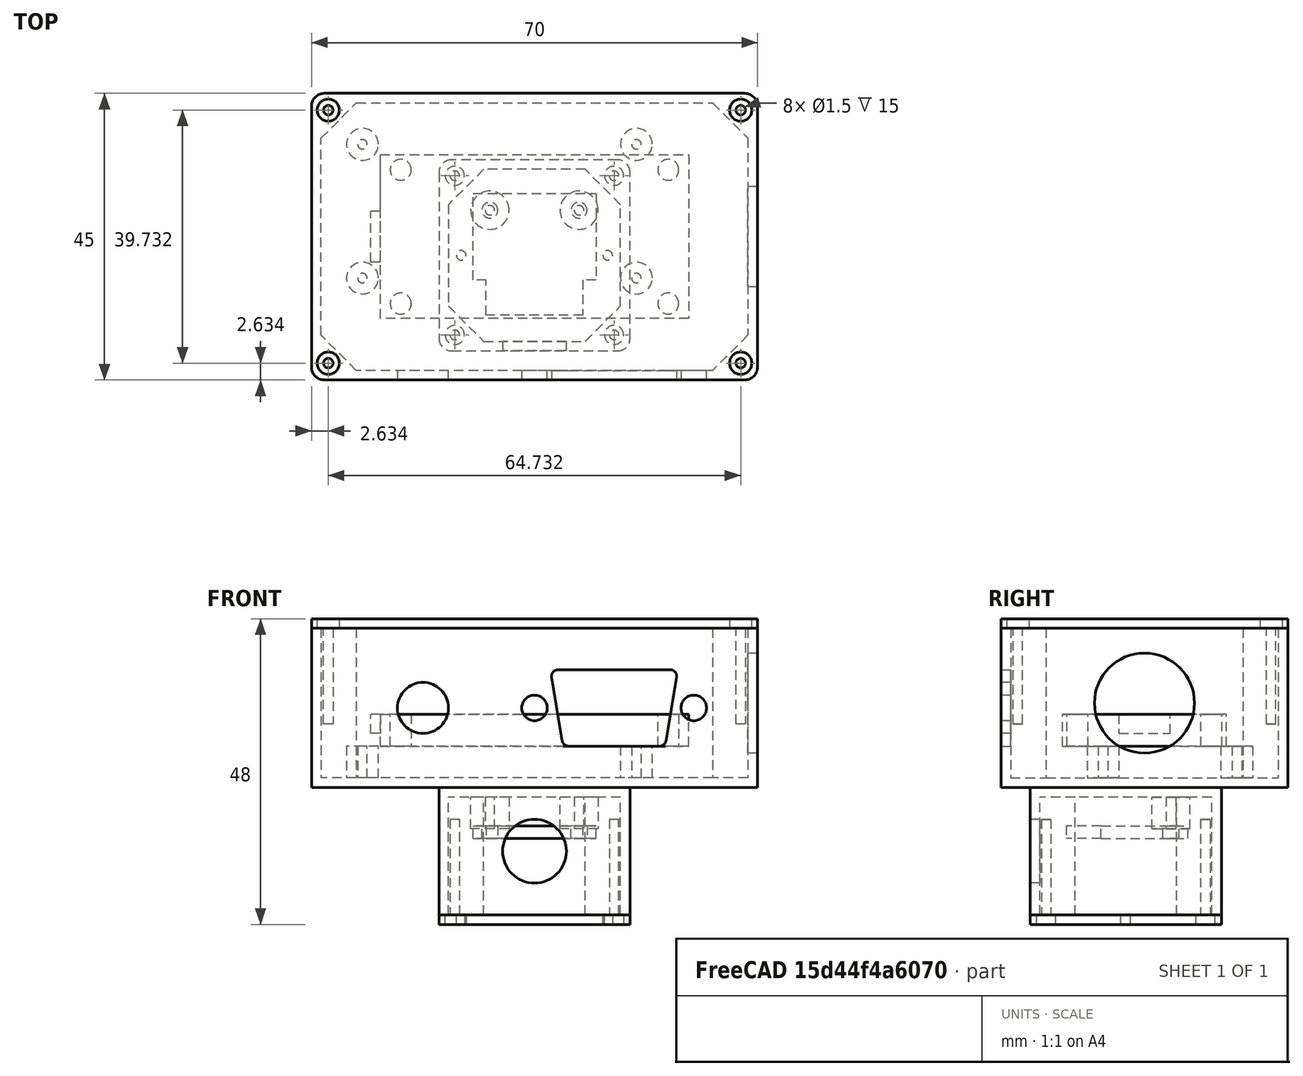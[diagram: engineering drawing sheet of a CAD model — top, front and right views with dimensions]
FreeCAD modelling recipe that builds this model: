
FCSTD DOCUMENT  (FreeCAD 0.18R4 (GitTag))
Label: BaroWifi
License: All rights reserved
LicenseURL: http://en.wikipedia.org/wiki/All_rights_reserved
objects: Sketcher::SketchObject×21, PartDesign::Pad×11, PartDesign::Pocket×10, PartDesign::Body×6, PartDesign::ShapeBinder×4, Mesh::Feature×4, PartDesign::Fillet×2, App::DocumentObjectGroup×2
note: 75 computed .brp shape members not serialized (recipe doc carries the construction recipe); baked Part::Feature solids carry a one-line shape summary decoded from their .brp

FEATURE [Sketcher::SketchObject] Sketch
  MapMode = 5
  Support = -> [XY_Plane]
  sketch-geometry (4):
    g0: LineSegment StartX=-24.2 StartY=12.85 StartZ=0 EndX=24.2 EndY=12.85 EndZ=0
    g1: LineSegment StartX=24.2 StartY=12.85 StartZ=0 EndX=24.2 EndY=-12.85 EndZ=0
    g2: LineSegment StartX=24.2 StartY=-12.85 StartZ=0 EndX=-24.2 EndY=-12.85 EndZ=0
    g3: LineSegment StartX=-24.2 StartY=-12.85 StartZ=0 EndX=-24.2 EndY=12.85 EndZ=0
  constraints (10):
    c: Coincident(g0,g1)
    c: Coincident(g1,g2)
    c: Coincident(g2,g3)
    c: Coincident(g3,g0)
    c: Horizontal(g2)
    c: Vertical(g1)
    c: Symmetric(g2,g0,g-1)
    c: Symmetric(g0,g0,g-2)
    c: DistanceX(g0,g0) = 48.4
    c: DistanceY(g1,g1) = 25.7
FEATURE [PartDesign::Pad] Pad
  Length = 5
  Length2 = 100
  Profile = -> Sketch
  Type = 0
FEATURE [Sketcher::SketchObject] Sketch001
  ExternalGeometry = -> [Pad]
  MapMode = 5
  Placement = pos=(-24.2,0,0) rot=(0.57735,-0.57735,-0.57735;2.0944rad)
  Support = -> [Pad]
  sketch-geometry (4):
    g0: LineSegment StartX=-4 StartY=5 StartZ=0 EndX=4 EndY=5 EndZ=0
    g1: LineSegment StartX=4 StartY=5 StartZ=0 EndX=4 EndY=2 EndZ=0
    g2: LineSegment StartX=4 StartY=2 StartZ=0 EndX=-4 EndY=2 EndZ=0
    g3: LineSegment StartX=-4 StartY=2 StartZ=0 EndX=-4 EndY=5 EndZ=0
  constraints (11):
    c: Coincident(g0,g1)
    c: Coincident(g1,g2)
    c: Coincident(g2,g3)
    c: Coincident(g3,g0)
    c: Horizontal(g2)
    c: Vertical(g1)
    c: Vertical(g3)
    c: Symmetric(g0,g0,g-2)
    c: PointOnObject(g0,g-3)
    c: DistanceY(g1,g1) = 3
    c: DistanceX(g2,g2) = 8
FEATURE [PartDesign::Pad] Pad001
  BaseFeature = -> Pad
  Length = 1.5
  Length2 = 100
  Profile = -> Sketch001
  Type = 0
FEATURE [Sketcher::SketchObject] Sketch002
  MapMode = 5
  Placement = pos=(0,0,5) rot=(0,0,1;0rad)
  Support = -> [Pad001]
  sketch-geometry (4):
    g0: Circle CenterX=-21 CenterY=10.5 CenterZ=0 NormalX=0 NormalY=0 NormalZ=1 AngleXU=0 Radius=1.65
    g1: Circle CenterX=-21 CenterY=-10.5 CenterZ=0 NormalX=0 NormalY=0 NormalZ=1 AngleXU=0 Radius=1.65
    g2: Circle CenterX=21 CenterY=10.5 CenterZ=0 NormalX=0 NormalY=0 NormalZ=1 AngleXU=0 Radius=1.65
    g3: Circle CenterX=21 CenterY=-10.5 CenterZ=0 NormalX=0 NormalY=0 NormalZ=1 AngleXU=0 Radius=1.65
  constraints (9):
    c: Symmetric(g0,g1,g-1)
    c: Symmetric(g2,g3,g-1)
    c: Symmetric(g0,g2,g-2)
    c: DistanceY(g1,g0) = 21
    c: Equal(g0,g2)
    c: Equal(g2,g3)
    c: Equal(g3,g1)
    c: Diameter(g0) = 3.3
    c: DistanceX(g0,g2) = 42
FEATURE [PartDesign::Pocket] Pocket
  BaseFeature = -> Pad001
  Length = 5
  Length2 = 100
  Profile = -> Sketch002
  Type = 1
FEATURE [PartDesign::Body] Body  label="NodeMCU"
  Group = -> [Sketch,Pad,Sketch001,Pad001,Sketch002,Pocket]
  Origin = -> Origin
  Placement = pos=(0,0,6.5) rot=(0,0,1;0rad)
  Tip = -> Pocket
FEATURE [Sketcher::SketchObject] Sketch003
  MapMode = 5
  Support = -> [XY_Plane001]
  sketch-geometry (4):
    g0: LineSegment StartX=-9.65 StartY=6.8 StartZ=0 EndX=9.65 EndY=6.8 EndZ=0
    g1: LineSegment StartX=9.65 StartY=6.8 StartZ=0 EndX=9.65 EndY=-6.8 EndZ=0
    g2: LineSegment StartX=9.65 StartY=-6.8 StartZ=0 EndX=-9.65 EndY=-6.8 EndZ=0
    g3: LineSegment StartX=-9.65 StartY=-6.8 StartZ=0 EndX=-9.65 EndY=6.8 EndZ=0
  constraints (10):
    c: Coincident(g0,g1)
    c: Coincident(g1,g2)
    c: Coincident(g2,g3)
    c: Coincident(g3,g0)
    c: Horizontal(g2)
    c: Vertical(g3)
    c: Symmetric(g0,g1,g-1)
    c: Symmetric(g0,g0,g-2)
    c: DistanceY(g3,g3) = 13.6
    c: DistanceX(g0,g0) = 19.3
FEATURE [PartDesign::Pad] Pad002
  Length = 2
  Length2 = 100
  Profile = -> Sketch003
  Type = 0
FEATURE [Sketcher::SketchObject] Sketch004
  ExternalGeometry = -> [Pad002]
  MapMode = 5
  Placement = pos=(0,0,2) rot=(0,0,1;0rad)
  Support = -> [Pad002]
  sketch-geometry (4):
    g0: LineSegment StartX=-7.6 StartY=-6.8 StartZ=0 EndX=7.6 EndY=-6.8 EndZ=0
    g1: LineSegment StartX=7.6 StartY=-6.8 StartZ=0 EndX=7.6 EndY=-12.3 EndZ=0
    g2: LineSegment StartX=7.6 StartY=-12.3 StartZ=0 EndX=-7.6 EndY=-12.3 EndZ=0
    g3: LineSegment StartX=-7.6 StartY=-12.3 StartZ=0 EndX=-7.6 EndY=-6.8 EndZ=0
  constraints (11):
    c: Coincident(g0,g1)
    c: Coincident(g1,g2)
    c: Coincident(g2,g3)
    c: Coincident(g3,g0)
    c: Horizontal(g2)
    c: Vertical(g1)
    c: Vertical(g3)
    c: PointOnObject(g0,g-3)
    c: Symmetric(g0,g0,g-2)
    c: DistanceY(g3,g3) = 5.5
    c: DistanceX(g2,g2) = 15.2
FEATURE [PartDesign::Pad] Pad003
  BaseFeature = -> Pad002
  Length = 2
  Length2 = 100
  Profile = -> Sketch004
  Reversed = true
  Type = 0
FEATURE [Sketcher::SketchObject] Sketch005
  ExternalGeometry = -> [Pad003]
  MapMode = 5
  Placement = pos=(0,0,2) rot=(0,0,1;0rad)
  Support = -> [Pad003]
  sketch-geometry (2):
    g0: Circle CenterX=-7 CenterY=4.15 CenterZ=0 NormalX=0 NormalY=0 NormalZ=1 AngleXU=0 Radius=1.25
    g1: Circle CenterX=7 CenterY=4.15 CenterZ=0 NormalX=0 NormalY=0 NormalZ=1 AngleXU=0 Radius=1.25
  constraints (5):
    c: Symmetric(g1,g0,g-2)
    c: Diameter(g0) = 2.5
    c: Equal(g0,g1)
    c: DistanceX(g0,g1) = 14
    c: DistanceY(g0,g-3) = 2.65
FEATURE [PartDesign::Pocket] Pocket001
  BaseFeature = -> Pad003
  Length = 5
  Length2 = 100
  Profile = -> Sketch005
  Type = 0
FEATURE [PartDesign::Body] Body001  label="BME680"
  Group = -> [Sketch003,Pad002,Sketch004,Pad003,Sketch005,Pocket001]
  Origin = -> Origin001
  Placement = pos=(0,0,-8) rot=(0,0,1;0rad)
  Tip = -> Pocket001
FEATURE [PartDesign::ShapeBinder] ReferencePocket
  Support = -> [Pocket]
  TraceSupport = false
FEATURE [Sketcher::SketchObject] Sketch006
  ExternalGeometry = -> [ReferencePocket]
  MapMode = 5
  Placement = pos=(0,0,0) rot=(1,0,0;3.14159rad)
  Support = -> [ReferencePocket]
  sketch-geometry (4):
    g0: LineSegment StartX=-35 StartY=22.5 StartZ=0 EndX=35 EndY=22.5 EndZ=0
    g1: LineSegment StartX=35 StartY=22.5 StartZ=0 EndX=35 EndY=-22.5 EndZ=0
    g2: LineSegment StartX=35 StartY=-22.5 StartZ=0 EndX=-35 EndY=-22.5 EndZ=0
    g3: LineSegment StartX=-35 StartY=-22.5 StartZ=0 EndX=-35 EndY=22.5 EndZ=0
  constraints (10):
    c: Coincident(g0,g1)
    c: Coincident(g1,g2)
    c: Coincident(g2,g3)
    c: Coincident(g3,g0)
    c: Horizontal(g2)
    c: Vertical(g3)
    c: Symmetric(g0,g0,g-2)
    c: Symmetric(g0,g1,g-1)
    c: DistanceX(g0,g0) = 70
    c: DistanceY(g1,g1) = 45
FEATURE [PartDesign::Pad] Pad004
  Length = 25
  Length2 = 100
  Profile = -> Sketch006
  Reversed = true
  Type = 0
FEATURE [Sketcher::SketchObject] Sketch007
  ExternalGeometry = -> [Pad004]
  MapMode = 5
  Placement = pos=(0,0,25) rot=(0,0,1;0rad)
  Support = -> [Pad004]
  sketch-geometry (10):
    g0: Circle [constr] CenterX=-32.5 CenterY=20 CenterZ=0 NormalX=0 NormalY=0 NormalZ=1 AngleXU=0 Radius=2.5
    g1: LineSegment StartX=-33.5 StartY=-15.4645 StartZ=0 EndX=-33.5 EndY=15.4645 EndZ=0
    g2: LineSegment StartX=-33.5 StartY=15.4645 StartZ=0 EndX=-27.9645 EndY=21 EndZ=0
    g3: LineSegment StartX=-27.9645 StartY=21 StartZ=0 EndX=27.9645 EndY=21 EndZ=0
    g4: LineSegment StartX=27.9645 StartY=21 StartZ=0 EndX=33.5 EndY=15.4645 EndZ=0
    g5: LineSegment StartX=33.5 StartY=15.4645 StartZ=0 EndX=33.5 EndY=-15.4645 EndZ=0
    g6: LineSegment StartX=33.5 StartY=-15.4645 StartZ=0 EndX=27.9645 EndY=-21 EndZ=0
    g7: LineSegment StartX=27.9645 StartY=-21 StartZ=0 EndX=-27.9645 EndY=-21 EndZ=0
    g8: LineSegment StartX=-27.9645 StartY=-21 StartZ=0 EndX=-33.5 EndY=-15.4645 EndZ=0
    g9: LineSegment [constr] StartX=-30.7322 StartY=18.2322 StartZ=0 EndX=-35 EndY=22.5 EndZ=0
  constraints (24):
    c: Diameter(g0) = 5
    c: Tangent(g0,g-3)
    c: Tangent(g0,g-4)
    c: Coincident(g1,g2)
    c: Coincident(g2,g3)
    c: Coincident(g3,g4)
    c: Coincident(g4,g5)
    c: Coincident(g5,g6)
    c: Coincident(g6,g7)
    c: Coincident(g7,g8)
    c: Coincident(g8,g1)
    c: Symmetric(g1,g1,g-1)
    c: Symmetric(g2,g7,g-1)
    c: Symmetric(g2,g3,g-2)
    c: Symmetric(g1,g4,g-2)
    c: Symmetric(g1,g5,g-2)
    c: Symmetric(g7,g6,g-2)
    c: Tangent(g2,g0)
    c: DistanceY(g2,g-4) = 1.5
    c: DistanceX(g-4,g1) = 1.5
    c: Coincident(g9,g-4)
    c: PointOnObject(g0,g9)
    c: PointOnObject(g9,g2)
    c: Perpendicular(g2,g9)
FEATURE [PartDesign::Pocket] Pocket002
  BaseFeature = -> Pad004
  Length = 23.5
  Length2 = 100
  Profile = -> Sketch007
  Type = 0
FEATURE [PartDesign::ShapeBinder] ReferencePocket001
  Support = -> [Pocket001]
  TraceSupport = false
FEATURE [Sketcher::SketchObject] Sketch014
  ExternalGeometry = -> [ReferencePocket001]
  MapMode = 5
  Placement = pos=(0,0,0) rot=(1,0,0;3.14159rad)
  Support = -> [ReferencePocket001]
  sketch-geometry (4):
    g0: LineSegment StartX=-15 StartY=17.9356 StartZ=0 EndX=15 EndY=17.9356 EndZ=0
    g1: LineSegment StartX=15 StartY=17.9356 StartZ=0 EndX=15 EndY=-12.0644 EndZ=0
    g2: LineSegment StartX=15 StartY=-12.0644 StartZ=0 EndX=-15 EndY=-12.0644 EndZ=0
    g3: LineSegment StartX=-15 StartY=-12.0644 StartZ=0 EndX=-15 EndY=17.9356 EndZ=0
  constraints (9):
    c: Coincident(g0,g1)
    c: Coincident(g1,g2)
    c: Coincident(g2,g3)
    c: Coincident(g3,g0)
    c: Vertical(g1)
    c: Symmetric(g1,g2,g-2)
    c: Symmetric(g0,g0,g-2)
    c: DistanceX(g0,g0) = 30
    c: DistanceY(g2,g0) = 30
FEATURE [PartDesign::Pad] Pad008
  Length = 20
  Length2 = 100
  Profile = -> Sketch014
  Type = 0
FEATURE [Sketcher::SketchObject] Sketch015
  ExternalGeometry = -> [Pad008]
  MapMode = 5
  Placement = pos=(0,0,-20) rot=(1,0,0;3.14159rad)
  Support = -> [Pad008]
  sketch-geometry (18):
    g0: LineSegment StartX=-13.5 StartY=-5.02884 StartZ=0 EndX=-13.5 EndY=10.9001 EndZ=0
    g1: LineSegment StartX=-13.5 StartY=10.9001 StartZ=0 EndX=-7.96447 EndY=16.4356 EndZ=0
    g2: LineSegment StartX=-7.96447 StartY=16.4356 StartZ=0 EndX=7.96447 EndY=16.4356 EndZ=0
    g3: LineSegment StartX=13.5 StartY=-5.02884 StartZ=0 EndX=7.96447 EndY=-10.5644 EndZ=0
    g4: LineSegment StartX=7.96447 StartY=-10.5644 StartZ=0 EndX=-7.96447 EndY=-10.5644 EndZ=0
    g5: LineSegment StartX=-7.96447 StartY=-10.5644 StartZ=0 EndX=-13.5 EndY=-5.02884 EndZ=0
    g6: LineSegment StartX=7.96447 StartY=16.4356 StartZ=0 EndX=13.5 EndY=10.9001 EndZ=0
    g7: LineSegment StartX=13.5 StartY=10.9001 StartZ=0 EndX=13.5 EndY=-5.02884 EndZ=0
    g8: LineSegment [constr] StartX=-15 StartY=2.93562 StartZ=0 EndX=15 EndY=2.93562 EndZ=0
    g9: LineSegment [constr] StartX=-15 StartY=2.93562 StartZ=0 EndX=-15 EndY=-12.0644 EndZ=0
    g10: LineSegment [constr] StartX=-15 StartY=17.9356 StartZ=0 EndX=-10.7322 EndY=13.6679 EndZ=0
    g11: LineSegment [constr] StartX=-13.5 StartY=10.9001 StartZ=0 EndX=-10.7322 EndY=13.6679 EndZ=0
    g12: LineSegment [constr] StartX=-10.7322 StartY=13.6679 StartZ=0 EndX=-7.96447 EndY=16.4356 EndZ=0
    g13: LineSegment [constr] StartX=-15 StartY=17.9356 StartZ=0 EndX=-6.46447 EndY=17.9356 EndZ=0
    g14: LineSegment [constr] StartX=-15 StartY=17.9356 StartZ=0 EndX=-15 EndY=9.40009 EndZ=0
    g15: LineSegment [constr] StartX=-15 StartY=9.40009 StartZ=0 EndX=-6.46447 EndY=17.9356 EndZ=0
    g16: LineSegment [constr] StartX=-15 StartY=17.9356 StartZ=0 EndX=-15 EndY=2.93562 EndZ=0
    g17: Circle [constr] CenterX=-12.5 CenterY=15.4356 CenterZ=0 NormalX=0 NormalY=0 NormalZ=1 AngleXU=0 Radius=2.5
  constraints (45):
    c: Coincident(g0,g1)
    c: Coincident(g1,g2)
    c: Coincident(g3,g4)
    c: Coincident(g4,g5)
    c: Coincident(g0,g5)
    c: Coincident(g6,g7)
    c: Coincident(g7,g3)
    c: Coincident(g6,g2)
    c: Perpendicular(g2,g7)
    c: Symmetric(g1,g2,g-2)
    c: Symmetric(g0,g6,g-2)
    c: PointOnObject(g9,g-5)
    c: Vertical(g9)
    c: PointOnObject(g8,g-6)
    c: PointOnObject(g8,g-4)
    c: Symmetric(g0,g0,g8)
    c: Symmetric(g1,g4,g8)
    c: Symmetric(g0,g3,g-2)
    c: Symmetric(g4,g3,g-2)
    c: DistanceY(g1,g10) = 1.5
    c: DistanceX(g10,g0) = 1.5
    c: PointOnObject(g10,g1)
    c: Perpendicular(g1,g10)
    c: Coincident(g11,g12)
    c: Equal(g12,g11)
    c: Coincident(g12,g1)
    c: Coincident(g11,g0)
    c: Coincident(g10,g11)
    c: Coincident(g15,g13)
    c: Coincident(g13,g14)
    c: Coincident(g14,g15)
    c: PointOnObject(g13,g-3)
    c: Equal(g14,g13)
    c: PointOnObject(g1,g15)
    c: Coincident(g10,g-6)
    c: Coincident(g10,g13)
    c: PointOnObject(g14,g-6)
    c: Coincident(g9,g8)
    c: Coincident(g16,g10)
    c: Coincident(g16,g8)
    c: Equal(g16,g9)
    c: Tangent(g13,g17)
    c: Tangent(g17,g14)
    c: Tangent(g1,g17)
    c: Diameter(g17) = 5
FEATURE [PartDesign::Pocket] Pocket006
  BaseFeature = -> Pad008
  Length = 18.5
  Length2 = 100
  Profile = -> Sketch015
  Type = 0
FEATURE [Sketcher::SketchObject] Sketch016
  ExternalGeometry = -> [ReferencePocket001]
  MapMode = 5
  Placement = pos=(0,0,0) rot=(1,0,0;3.14159rad)
  Support = -> [ReferencePocket001]
  sketch-geometry (2):
    g0: Circle CenterX=-7 CenterY=-4.15 CenterZ=0 NormalX=0 NormalY=0 NormalZ=1 AngleXU=0 Radius=3
    g1: Circle CenterX=7 CenterY=-4.15 CenterZ=0 NormalX=0 NormalY=0 NormalZ=1 AngleXU=0 Radius=3
  constraints (4):
    c: Coincident(g0,g-3)
    c: Coincident(g1,g-4)
    c: Equal(g0,g1)
    c: Diameter(g0) = 6
FEATURE [PartDesign::Pad] Pad009
  BaseFeature = -> Pocket006
  Length = 6.5
  Length2 = 100
  Profile = -> Sketch016
  Type = 0
FEATURE [Sketcher::SketchObject] Sketch017
  ExternalGeometry = -> [Pad009]
  MapMode = 5
  Placement = pos=(0,0,-6.5) rot=(1,0,0;3.14159rad)
  Support = -> [Pad009]
  sketch-geometry (2):
    g0: Circle CenterX=-7 CenterY=-4.15 CenterZ=0 NormalX=0 NormalY=0 NormalZ=1 AngleXU=0 Radius=0.75
    g1: Circle CenterX=7 CenterY=-4.15 CenterZ=0 NormalX=0 NormalY=0 NormalZ=1 AngleXU=0 Radius=0.75
  constraints (4):
    c: Coincident(g0,g-4)
    c: Coincident(g1,g-3)
    c: Equal(g1,g0)
    c: Diameter(g0) = 1.5
FEATURE [PartDesign::Pocket] Pocket007
  BaseFeature = -> Pad009
  Length = 5
  Length2 = 100
  Profile = -> Sketch017
  Type = 0
FEATURE [Sketcher::SketchObject] Sketch018
  ExternalGeometry = -> [Pocket007]
  MapMode = 5
  Placement = pos=(0,0,-20) rot=(1,0,0;3.14159rad)
  Support = -> [Pocket007]
  sketch-geometry (8):
    g0: Circle [constr] CenterX=-12.5 CenterY=15.4356 CenterZ=0 NormalX=0 NormalY=0 NormalZ=1 AngleXU=0 Radius=2.5
    g1: Circle CenterX=-12.5 CenterY=15.4356 CenterZ=0 NormalX=0 NormalY=0 NormalZ=1 AngleXU=0 Radius=0.75
    g2: Circle [constr] CenterX=12.5 CenterY=15.4356 CenterZ=0 NormalX=0 NormalY=0 NormalZ=1 AngleXU=0 Radius=2.5
    g3: Circle [constr] CenterX=12.5 CenterY=-9.56438 CenterZ=0 NormalX=0 NormalY=0 NormalZ=1 AngleXU=0 Radius=2.5
    g4: Circle [constr] CenterX=-12.5 CenterY=-9.56438 CenterZ=0 NormalX=0 NormalY=0 NormalZ=1 AngleXU=0 Radius=2.5
    g5: Circle CenterX=12.5 CenterY=15.4356 CenterZ=0 NormalX=0 NormalY=0 NormalZ=1 AngleXU=0 Radius=0.75
    g6: Circle CenterX=12.5 CenterY=-9.56438 CenterZ=0 NormalX=0 NormalY=0 NormalZ=1 AngleXU=0 Radius=0.75
    g7: Circle CenterX=-12.5 CenterY=-9.56438 CenterZ=0 NormalX=0 NormalY=0 NormalZ=1 AngleXU=0 Radius=0.75
  constraints (20):
    c: Tangent(g0,g-3)
    c: Tangent(g0,g-5)
    c: Tangent(g0,g-4)
    c: Coincident(g1,g0)
    c: Tangent(g4,g-8)
    c: Tangent(g4,g-7)
    c: Tangent(g4,g-5)
    c: Tangent(g3,g-9)
    c: Tangent(g3,g-7)
    c: Tangent(g3,g-6)
    c: Tangent(g2,g-10)
    c: Tangent(g2,g-3)
    c: Tangent(g2,g-6)
    c: Coincident(g7,g4)
    c: Coincident(g5,g2)
    c: Coincident(g6,g3)
    c: Equal(g6,g5)
    c: Equal(g5,g1)
    c: Equal(g1,g7)
    c: Diameter(g1) = 1.5
FEATURE [PartDesign::Pocket] Pocket008
  BaseFeature = -> Pocket007
  Length = 15
  Length2 = 100
  Profile = -> Sketch018
  Type = 0
FEATURE [PartDesign::ShapeBinder] ReferenceFillet001
  TraceSupport = false
FEATURE [Sketcher::SketchObject] Sketch020
  ExternalGeometry = -> [ReferenceFillet001]
  MapMode = 5
  Placement = pos=(0,0,-20) rot=(1,0,0;3.14159rad)
  Support = -> [ReferenceFillet001]
  sketch-geometry (17):
    g0: LineSegment StartX=-13 StartY=17.9356 StartZ=0 EndX=13 EndY=17.9356 EndZ=0
    g1: LineSegment StartX=15 StartY=15.9356 StartZ=0 EndX=15 EndY=-10.0644 EndZ=0
    g2: LineSegment StartX=13 StartY=-12.0644 StartZ=0 EndX=-13 EndY=-12.0644 EndZ=0
    g3: LineSegment StartX=-15 StartY=-10.0644 StartZ=0 EndX=-15 EndY=15.9356 EndZ=0
    g4: ArcOfCircle CenterX=-13 CenterY=15.9356 CenterZ=0 NormalX=0 NormalY=0 NormalZ=1 AngleXU=0 Radius=2 StartAngle=1.5708 EndAngle=3.14159
    g5: ArcOfCircle CenterX=13 CenterY=15.9356 CenterZ=0 NormalX=0 NormalY=0 NormalZ=1 AngleXU=0 Radius=2 StartAngle=0 EndAngle=1.5708
    g6: ArcOfCircle CenterX=13 CenterY=-10.0644 CenterZ=0 NormalX=0 NormalY=0 NormalZ=1 AngleXU=0 Radius=2 StartAngle=4.71239 EndAngle=6.28319
    g7: ArcOfCircle CenterX=-13 CenterY=-10.0644 CenterZ=0 NormalX=0 NormalY=0 NormalZ=1 AngleXU=0 Radius=2 StartAngle=3.14159 EndAngle=4.71239
    g8: Circle CenterX=-12.5 CenterY=15.4356 CenterZ=0 NormalX=0 NormalY=0 NormalZ=1 AngleXU=0 Radius=1.5
    g9: Circle CenterX=12.5 CenterY=15.4356 CenterZ=0 NormalX=0 NormalY=0 NormalZ=1 AngleXU=0 Radius=1.5
    g10: Circle CenterX=12.5 CenterY=-9.56438 CenterZ=0 NormalX=0 NormalY=0 NormalZ=1 AngleXU=0 Radius=1.5
    g11: Circle CenterX=-12.5 CenterY=-9.56438 CenterZ=0 NormalX=0 NormalY=0 NormalZ=1 AngleXU=0 Radius=1.5
    g12: Circle CenterX=-11.5 CenterY=2.93562 CenterZ=0 NormalX=0 NormalY=0 NormalZ=1 AngleXU=0 Radius=0.75
    g13: Circle CenterX=11.5 CenterY=2.93562 CenterZ=0 NormalX=0 NormalY=0 NormalZ=1 AngleXU=0 Radius=0.75
    g14: LineSegment [constr] StartX=-13 StartY=17.9356 StartZ=0 EndX=-13 EndY=2.93562 EndZ=0
    g15: LineSegment [constr] StartX=-13 StartY=2.93562 StartZ=0 EndX=-13 EndY=-12.0644 EndZ=0
    g16: LineSegment [constr] StartX=-13 StartY=2.93562 StartZ=0 EndX=15 EndY=2.93562 EndZ=0
  constraints (41):
    c: Coincident(g7,g3)
    c: Coincident(g3,g4)
    c: Coincident(g4,g0)
    c: Coincident(g0,g5)
    c: Coincident(g5,g1)
    c: Coincident(g1,g6)
    c: Coincident(g6,g2)
    c: Coincident(g2,g7)
    c: Coincident(g7,g-12)
    c: Coincident(g4,g-4)
    c: Coincident(g5,g-9)
    c: Coincident(g6,g-10)
    c: Coincident(g0,g-4)
    c: Coincident(g1,g-9)
    c: Coincident(g1,g-10)
    c: Coincident(g2,g-12)
    c: PointOnObject(g3,g-7)
    c: PointOnObject(g0,g-3)
    c: PointOnObject(g2,g-11)
    c: PointOnObject(g3,g-7)
    c: Coincident(g8,g-6)
    c: Coincident(g9,g-16)
    c: Coincident(g10,g-15)
    c: Coincident(g11,g-13)
    c: Equal(g11,g8)
    c: Equal(g8,g9)
    c: Equal(g9,g10)
    c: Diameter(g8) = 3
    c: Equal(g12,g13)
    c: Diameter(g12) = 1.5
    c: Symmetric(g12,g13,g-2)
    c: Coincident(g14,g15)
    c: Equal(g14,g15)
    c: Parallel(g14,g15)
    c: Coincident(g14,g0)
    c: Coincident(g15,g2)
    c: Coincident(g16,g14)
    c: PointOnObject(g16,g1)
    c: Perpendicular(g14,g16)
    c: PointOnObject(g13,g16)
    c: DistanceX(g12,g13) = 23
FEATURE [PartDesign::Pad] Pad010
  Length = 1.5
  Length2 = 100
  Profile = -> Sketch020
  Type = 0
FEATURE [PartDesign::Body] Body005  label="Capot BME"
  Group = -> [ReferenceFillet001,Sketch020,Pad010]
  Origin = -> Origin005
  Tip = -> Pad010
FEATURE [Mesh::Feature] Mesh003  label="Capot BME (Meshed)"
FEATURE [Sketcher::SketchObject] Sketch008
  ExternalGeometry = -> [Pocket002]
  MapMode = 5
  Placement = pos=(0,0,0) rot=(1,0,0;3.14159rad)
  Support = -> [ReferencePocket]
  sketch-geometry (12):
    g0: Circle CenterX=-27 CenterY=6.5 CenterZ=0 NormalX=0 NormalY=0 NormalZ=1 AngleXU=0 Radius=0.75
    g1: Circle CenterX=16 CenterY=6.5 CenterZ=0 NormalX=0 NormalY=0 NormalZ=1 AngleXU=0 Radius=0.75
    g2: Circle CenterX=-27 CenterY=-14.5 CenterZ=0 NormalX=0 NormalY=0 NormalZ=1 AngleXU=0 Radius=0.75
    g3: Circle CenterX=16 CenterY=-14.5 CenterZ=0 NormalX=0 NormalY=0 NormalZ=1 AngleXU=0 Radius=0.75
    g4: LineSegment [constr] StartX=-27 StartY=6.5 StartZ=0 EndX=16 EndY=6.5 EndZ=0
    g5: LineSegment [constr] StartX=16 StartY=6.5 StartZ=0 EndX=16 EndY=-14.5 EndZ=0
    g6: LineSegment [constr] StartX=16 StartY=-14.5 StartZ=0 EndX=-27 EndY=-14.5 EndZ=0
    g7: LineSegment [constr] StartX=-27 StartY=-14.5 StartZ=0 EndX=-27 EndY=6.5 EndZ=0
    g8: Circle CenterX=-27 CenterY=6.5 CenterZ=0 NormalX=0 NormalY=0 NormalZ=1 AngleXU=0 Radius=2.5
    g9: Circle CenterX=16 CenterY=6.5 CenterZ=0 NormalX=0 NormalY=0 NormalZ=1 AngleXU=0 Radius=2.5
    g10: Circle CenterX=16 CenterY=-14.5 CenterZ=0 NormalX=0 NormalY=0 NormalZ=1 AngleXU=0 Radius=2.5
    g11: Circle CenterX=-27 CenterY=-14.5 CenterZ=0 NormalX=0 NormalY=0 NormalZ=1 AngleXU=0 Radius=2.5
  constraints (28):
    c: Equal(g0,g1)
    c: Equal(g1,g2)
    c: Equal(g2,g3)
    c: Coincident(g4,g5)
    c: Coincident(g5,g6)
    c: Coincident(g6,g7)
    c: Coincident(g7,g4)
    c: Horizontal(g4)
    c: Horizontal(g6)
    c: Vertical(g5)
    c: Vertical(g7)
    c: DistanceX(g4,g4) = 43
    c: DistanceY(g7,g7) = 21
    c: Coincident(g4,g0)
    c: Coincident(g1,g4)
    c: Coincident(g3,g5)
    c: Coincident(g2,g6)
    c: Diameter(g0) = 1.5
    c: Equal(g8,g9)
    c: Equal(g9,g10)
    c: Equal(g10,g11)
    c: Diameter(g8) = 5
    c: Coincident(g8,g0)
    c: Coincident(g9,g1)
    c: Coincident(g10,g3)
    c: Coincident(g11,g2)
    c: DistanceX(g-4,g2) = 8
    c: DistanceY(g-4,g2) = 8
FEATURE [PartDesign::Pad] Pad005
  BaseFeature = -> Pocket002
  Length = 6.5
  Length2 = 100
  Profile = -> Sketch008
  Reversed = true
  Type = 0
FEATURE [Sketcher::SketchObject] Sketch009
  ExternalGeometry = -> [Pad005]
  MapMode = 5
  Placement = pos=(33.5,0,0) rot=(0.57735,-0.57735,-0.57735;2.0944rad)
  Support = -> [Pad005]
  sketch-geometry (4):
    g0: Circle CenterX=-5e-16 CenterY=13.25 CenterZ=0 NormalX=0 NormalY=0 NormalZ=1 AngleXU=0 Radius=7.85
    g1: LineSegment [constr] StartX=15.4645 StartY=25 StartZ=0 EndX=-15.4645 EndY=1.5 EndZ=0
    g2: LineSegment [constr] StartX=-15.4645 StartY=25 StartZ=0 EndX=15.4645 EndY=1.5 EndZ=0
    g3: GeomPoint X=-5e-16 Y=13.25 Z=0
  constraints (8):
    c: Coincident(g0,g3)
    c: Diameter(g0) = 15.7
    c: PointOnObject(g0,g2)
    c: PointOnObject(g0,g1)
    c: Coincident(g2,g-5)
    c: Coincident(g1,g-6)
    c: Coincident(g2,g-6)
    c: Coincident(g1,g-5)
FEATURE [PartDesign::Pocket] Pocket003
  BaseFeature = -> Pad005
  Length = 5
  Length2 = 100
  Profile = -> Sketch009
  Type = 0
FEATURE [Sketcher::SketchObject] Sketch010
  ExternalGeometry = -> [Pocket003]
  MapMode = 5
  Placement = pos=(0,-22.5,0) rot=(1,0,0;1.5708rad)
  Support = -> [Pocket003]
  sketch-geometry (16):
    g0: GeomPoint X=0 Y=25 Z=0
    g1: LineSegment [constr] StartX=-35 StartY=25 StartZ=0 EndX=0 EndY=0 EndZ=0
    g2: LineSegment [constr] StartX=0 StartY=25 StartZ=0 EndX=-35 EndY=0 EndZ=0
    g3: GeomPoint X=-17.5 Y=12.5 Z=0
    g4: Circle CenterX=-17.5 CenterY=12.5 CenterZ=0 NormalX=0 NormalY=0 NormalZ=1 AngleXU=0 Radius=4
    g5: LineSegment [constr] StartX=0 StartY=25 StartZ=0 EndX=35 EndY=0 EndZ=0
    g6: LineSegment [constr] StartX=35 StartY=25 StartZ=0 EndX=0 EndY=0 EndZ=0
    g7: LineSegment [constr] StartX=12.5 StartY=25 StartZ=0 EndX=12.5 EndY=0 EndZ=0
    g8: LineSegment StartX=2.5 StartY=18.5 StartZ=0 EndX=22.5 EndY=18.5 EndZ=0
    g9: LineSegment StartX=22.5 StartY=18.5 StartZ=0 EndX=20.5 EndY=6.5 EndZ=0
    g10: LineSegment StartX=20.5 StartY=6.5 StartZ=0 EndX=4.5 EndY=6.5 EndZ=0
    g11: LineSegment StartX=4.5 StartY=6.5 StartZ=0 EndX=2.5 EndY=18.5 EndZ=0
    g12: Circle CenterX=0 CenterY=12.5 CenterZ=0 NormalX=0 NormalY=0 NormalZ=1 AngleXU=0 Radius=2
    g13: Circle CenterX=25 CenterY=12.5 CenterZ=0 NormalX=0 NormalY=0 NormalZ=1 AngleXU=0 Radius=2
    g14: LineSegment [constr] StartX=2.5 StartY=6.5 StartZ=0 EndX=22.5 EndY=6.5 EndZ=0
    g15: LineSegment [constr] StartX=0 StartY=12.5 StartZ=0 EndX=25 EndY=12.5 EndZ=0
  constraints (37):
    c: PointOnObject(g0,g-2)
    c: PointOnObject(g0,g-3)
    c: Coincident(g1,g-4)
    c: Coincident(g0,g2)
    c: Coincident(g1,g-1)
    c: Coincident(g2,g-4)
    c: PointOnObject(g3,g2)
    c: PointOnObject(g3,g1)
    c: Coincident(g4,g3)
    c: Diameter(g4) = 8
    c: Coincident(g5,g0)
    c: Coincident(g6,g-3)
    c: Coincident(g5,g-5)
    c: Coincident(g6,g-1)
    c: PointOnObject(g7,g-3)
    c: PointOnObject(g7,g-1)
    c: Coincident(g8,g9)
    c: Coincident(g9,g10)
    c: Coincident(g10,g11)
    c: Coincident(g11,g8)
    c: Symmetric(g8,g8,g7)
    c: Symmetric(g10,g9,g7)
    c: Symmetric(g12,g13,g7)
    c: Equal(g12,g13)
    c: Diameter(g12) = 4
    c: DistanceX(g12,g13) = 25
    c: DistanceX(g8,g8) = 20
    c: DistanceX(g10,g9) = 16
    c: DistanceY(g9,g8) = 12
    c: PointOnObject(g10,g14)
    c: PointOnObject(g12,g-2)
    c: Parallel(g8,g-3)
    c: Coincident(g15,g13)
    c: Coincident(g15,g12)
    c: Symmetric(g8,g14,g15)
    c: Symmetric(g8,g14,g15)
    c: PointOnObject(g3,g15)
FEATURE [PartDesign::Pocket] Pocket004
  BaseFeature = -> Pocket003
  Length = 5
  Length2 = 100
  Profile = -> Sketch010
  Type = 0
FEATURE [Sketcher::SketchObject] Sketch011
  ExternalGeometry = -> [Pocket004]
  MapMode = 5
  Placement = pos=(0,-22.5,0) rot=(1,0,0;1.5708rad)
  Support = -> [Pocket004]
  sketch-geometry (12):
    g0: ArcOfCircle CenterX=21.3195 CenterY=17.5 CenterZ=0 NormalX=0 NormalY=0 NormalZ=1 AngleXU=0 Radius=1 StartAngle=6.11804 EndAngle=7.85398
    g1: ArcOfCircle CenterX=3.68046 CenterY=17.5 CenterZ=0 NormalX=0 NormalY=0 NormalZ=1 AngleXU=0 Radius=1 StartAngle=1.5708 EndAngle=3.30674
    g2: ArcOfCircle CenterX=5.34713 CenterY=7.5 CenterZ=0 NormalX=0 NormalY=0 NormalZ=1 AngleXU=0 Radius=1 StartAngle=3.30675 EndAngle=4.71238
    g3: ArcOfCircle CenterX=19.6529 CenterY=7.5 CenterZ=0 NormalX=0 NormalY=0 NormalZ=1 AngleXU=0 Radius=1 StartAngle=4.71239 EndAngle=6.11804
    g4: LineSegment StartX=21.3195 StartY=18.5 StartZ=0 EndX=22.5 EndY=18.5 EndZ=0
    g5: LineSegment StartX=22.5 StartY=18.5 StartZ=0 EndX=22.3059 EndY=17.3356 EndZ=0
    g6: LineSegment StartX=20.6393 StartY=7.3356 StartZ=0 EndX=20.5 EndY=6.5 EndZ=0
    g7: LineSegment StartX=20.5 StartY=6.5 StartZ=0 EndX=19.6529 EndY=6.5 EndZ=0
    g8: LineSegment StartX=4.36073 StartY=7.33559 StartZ=0 EndX=4.5 EndY=6.5 EndZ=0
    g9: LineSegment StartX=4.5 StartY=6.5 StartZ=0 EndX=5.34712 EndY=6.5 EndZ=0
    g10: LineSegment StartX=3.68046 StartY=18.5 StartZ=0 EndX=2.5 EndY=18.5 EndZ=0
    g11: LineSegment StartX=2.5 StartY=18.5 StartZ=0 EndX=2.69407 EndY=17.3356 EndZ=0
  constraints (34):
    c: Radius(g0) = 1
    c: Equal(g1,g0)
    c: Equal(g0,g3)
    c: Equal(g3,g2)
    c: PointOnObject(g1,g-3)
    c: PointOnObject(g1,g-4)
    c: PointOnObject(g0,g-3)
    c: PointOnObject(g0,g-6)
    c: PointOnObject(g3,g-6)
    c: PointOnObject(g2,g-5)
    c: PointOnObject(g2,g-4)
    c: Coincident(g5,g-6)
    c: Coincident(g5,g4)
    c: Coincident(g4,g0)
    c: Coincident(g5,g0)
    c: Equal(g5,g4)
    c: Coincident(g7,g3)
    c: Coincident(g7,g6)
    c: Coincident(g7,g-6)
    c: Equal(g6,g7)
    c: Coincident(g9,g2)
    c: Coincident(g9,g8)
    c: Coincident(g9,g-5)
    c: Coincident(g8,g2)
    c: Equal(g8,g9)
    c: Coincident(g11,g-4)
    c: Coincident(g11,g10)
    c: Equal(g10,g11)
    c: Tangent(g10,g1) = -1.5708
    c: Tangent(g11,g1) = -1.5708
    c: Tangent(g0,g-3)
    c: Tangent(g6,g3) = 1.5708
    c: Tangent(g-5,g3)
    c: Tangent(g2,g-4)
FEATURE [PartDesign::Pad] Pad006
  BaseFeature = -> Pocket004
  Length = 1.5
  Length2 = 100
  Profile = -> Sketch011
  Reversed = true
  Type = 0
FEATURE [PartDesign::Fillet] Fillet
  Base = -> Pad006 [Edge4,Edge1,Edge39,Edge20]
  BaseFeature = -> Pad006
  Radius = 2
FEATURE [Sketcher::SketchObject] Sketch012
  ExternalGeometry = -> [Fillet]
  MapMode = 5
  Placement = pos=(0,0,25) rot=(0,0,1;0rad)
  Support = -> [Fillet]
  sketch-geometry (9):
    g0: LineSegment [constr] StartX=-33 StartY=22.5 StartZ=0 EndX=-27.9645 EndY=21 EndZ=0
    g1: LineSegment [constr] StartX=-33 StartY=22.5 StartZ=0 EndX=-35 EndY=20.5 EndZ=0
    g2: LineSegment [constr] StartX=-35 StartY=20.5 StartZ=0 EndX=-33.5 EndY=15.4645 EndZ=0
    g3: LineSegment [constr] StartX=-30.7322 StartY=18.2322 StartZ=0 EndX=-32.3661 EndY=19.8661 EndZ=0
    g4: LineSegment [constr] StartX=-32.3661 StartY=19.8661 StartZ=0 EndX=-34 EndY=21.5 EndZ=0
    g5: Circle CenterX=-32.3661 CenterY=19.8661 CenterZ=0 NormalX=0 NormalY=0 NormalZ=1 AngleXU=0 Radius=0.75
    g6: Circle CenterX=32.3661 CenterY=19.8661 CenterZ=0 NormalX=0 NormalY=0 NormalZ=1 AngleXU=0 Radius=0.75
    g7: Circle CenterX=32.3661 CenterY=-19.8661 CenterZ=0 NormalX=0 NormalY=0 NormalZ=1 AngleXU=0 Radius=0.75
    g8: Circle CenterX=-32.3661 CenterY=-19.8661 CenterZ=0 NormalX=0 NormalY=0 NormalZ=1 AngleXU=0 Radius=0.75
  constraints (21):
    c: Coincident(g1,g0)
    c: Coincident(g0,g-6)
    c: Coincident(g2,g1)
    c: Coincident(g2,g-6)
    c: Coincident(g2,g-4)
    c: Coincident(g0,g-4)
    c: Coincident(g3,g4)
    c: PointOnObject(g4,g1)
    c: Parallel(g4,g3)
    c: PointOnObject(g-6,g4)
    c: PointOnObject(g3,g-4)
    c: Equal(g3,g4)
    c: Perpendicular(g-4,g3)
    c: Equal(g8,g7)
    c: Equal(g7,g6)
    c: Equal(g6,g5)
    c: Diameter(g5) = 1.5
    c: Coincident(g5,g3)
    c: Symmetric(g5,g6,g-2)
    c: Symmetric(g5,g8,g-1)
    c: Symmetric(g8,g7,g-2)
FEATURE [PartDesign::Pocket] Pocket005
  BaseFeature = -> Fillet
  Length = 15
  Length2 = 100
  Profile = -> Sketch012
  Type = 0
FEATURE [PartDesign::Body] Body002  label="CorpsBoiteMCU"
  Group = -> [ReferencePocket,Sketch006,Pad004,Sketch007,Pocket002,Sketch008,Pad005,Sketch009,Pocket003,Sketch010,Pocket004,Sketch011,Pad006,Fillet,Sketch012,Pocket005]
  Origin = -> Origin002
  Tip = -> Pocket005
FEATURE [PartDesign::ShapeBinder] ReferencePocket005
  Support = -> [Pocket005]
  TraceSupport = false
FEATURE [Sketcher::SketchObject] Sketch013
  ExternalGeometry = -> [ReferencePocket005]
  MapMode = 5
  Placement = pos=(0,0,25) rot=(0,0,1;0rad)
  Support = -> [ReferencePocket005]
  sketch-geometry (12):
    g0: LineSegment StartX=-33 StartY=22.5 StartZ=0 EndX=33 EndY=22.5 EndZ=0
    g1: LineSegment StartX=35 StartY=20.5 StartZ=0 EndX=35 EndY=-20.5 EndZ=0
    g2: LineSegment StartX=33 StartY=-22.5 StartZ=0 EndX=-33 EndY=-22.5 EndZ=0
    g3: LineSegment StartX=-35 StartY=-20.5 StartZ=0 EndX=-35 EndY=20.5 EndZ=0
    g4: ArcOfCircle CenterX=-33 CenterY=20.5 CenterZ=0 NormalX=0 NormalY=0 NormalZ=1 AngleXU=0 Radius=2 StartAngle=1.5708 EndAngle=3.14159
    g5: ArcOfCircle CenterX=33 CenterY=20.5 CenterZ=0 NormalX=0 NormalY=0 NormalZ=1 AngleXU=0 Radius=2 StartAngle=6.28318 EndAngle=7.85398
    g6: ArcOfCircle CenterX=33 CenterY=-20.5 CenterZ=0 NormalX=0 NormalY=0 NormalZ=1 AngleXU=0 Radius=2 StartAngle=4.71238 EndAngle=6.28319
    g7: ArcOfCircle CenterX=-33 CenterY=-20.5 CenterZ=0 NormalX=0 NormalY=0 NormalZ=1 AngleXU=0 Radius=2 StartAngle=3.14159 EndAngle=4.71239
    g8: Circle CenterX=-32.3661 CenterY=19.8661 CenterZ=0 NormalX=0 NormalY=0 NormalZ=1 AngleXU=0 Radius=1.75
    g9: Circle CenterX=32.3661 CenterY=19.8661 CenterZ=0 NormalX=0 NormalY=0 NormalZ=1 AngleXU=0 Radius=1.75
    g10: Circle CenterX=-32.3661 CenterY=-19.8661 CenterZ=0 NormalX=0 NormalY=0 NormalZ=1 AngleXU=0 Radius=1.75
    g11: Circle CenterX=32.3661 CenterY=-19.8661 CenterZ=0 NormalX=0 NormalY=0 NormalZ=1 AngleXU=0 Radius=1.75
  constraints (28):
    c: Coincident(g7,g3)
    c: Coincident(g7,g2)
    c: Coincident(g2,g6)
    c: Coincident(g6,g1)
    c: Coincident(g1,g5)
    c: Coincident(g5,g0)
    c: Coincident(g0,g4)
    c: Coincident(g4,g3)
    c: Coincident(g-5,g4)
    c: Coincident(g5,g-9)
    c: Coincident(g6,g-12)
    c: PointOnObject(g0,g-4)
    c: Coincident(g3,g-6)
    c: Coincident(g0,g-9)
    c: PointOnObject(g1,g-10)
    c: Coincident(g1,g-12)
    c: PointOnObject(g2,g-11)
    c: Coincident(g2,g-13)
    c: PointOnObject(g3,g-6)
    c: Coincident(g7,g-13)
    c: Coincident(g8,g-3)
    c: Coincident(g9,g-8)
    c: Coincident(g11,g-16)
    c: Coincident(g10,g-15)
    c: Equal(g10,g11)
    c: Equal(g11,g9)
    c: Equal(g9,g8)
    c: Diameter(g8) = 3.5
FEATURE [PartDesign::Pad] Pad007
  Length = 1.5
  Length2 = 100
  Profile = -> Sketch013
  Type = 0
FEATURE [PartDesign::Body] Body003  label="CapotMCU"
  Group = -> [ReferencePocket005,Sketch013,Pad007]
  Origin = -> Origin003
  Tip = -> Pad007
FEATURE [App::DocumentObjectGroup] Group  label="GoupeNodeMCU"
  Group = -> [Body003,Body002,Body]
FEATURE [Mesh::Feature] Mesh  label="CapotMCU (Meshed)"
FEATURE [Mesh::Feature] Mesh006  label="CorpsBoiteMCU (Meshed)"
FEATURE [Sketcher::SketchObject] Sketch021
  ExternalGeometry = -> [Pocket008]
  MapMode = 5
  Placement = pos=(0,-17.9356,0) rot=(1,0,0;1.5708rad)
  Support = -> [Pocket008]
  sketch-geometry (3):
    g0: LineSegment [constr] StartX=-15 StartY=0 StartZ=0 EndX=15 EndY=-20 EndZ=0
    g1: LineSegment [constr] StartX=15 StartY=0 StartZ=0 EndX=-15 EndY=-20 EndZ=0
    g2: Circle CenterX=-5e-16 CenterY=-10 CenterZ=0 NormalX=0 NormalY=0 NormalZ=1 AngleXU=0 Radius=5
  constraints (7):
    c: Coincident(g0,g-3)
    c: Coincident(g1,g-5)
    c: Coincident(g1,g-4)
    c: Coincident(g0,g-5)
    c: Diameter(g2) = 10
    c: PointOnObject(g2,g1)
    c: PointOnObject(g2,g0)
FEATURE [PartDesign::Pocket] Pocket009
  BaseFeature = -> Pocket008
  Length = 5
  Length2 = 100
  Profile = -> Sketch021
  Type = 0
FEATURE [PartDesign::Fillet] Fillet001
  Base = -> Pocket009 [Edge4,Edge27,Edge1,Edge6]
  BaseFeature = -> Pocket009
  Radius = 2
FEATURE [PartDesign::Body] Body004  label="Boite BME"
  Group = -> [ReferencePocket001,Sketch014,Pad008,Sketch015,Pocket006,Sketch016,Pad009,Sketch017,Pocket007,Sketch018,Pocket008,Sketch021,Pocket009,Fillet001]
  Origin = -> Origin004
  Tip = -> Fillet001
FEATURE [App::DocumentObjectGroup] Group001  label="GroupeBME680"
  Group = -> [Body001,Body004,Body005]
FEATURE [Mesh::Feature] Mesh007  label="Boite BME (Meshed)"
